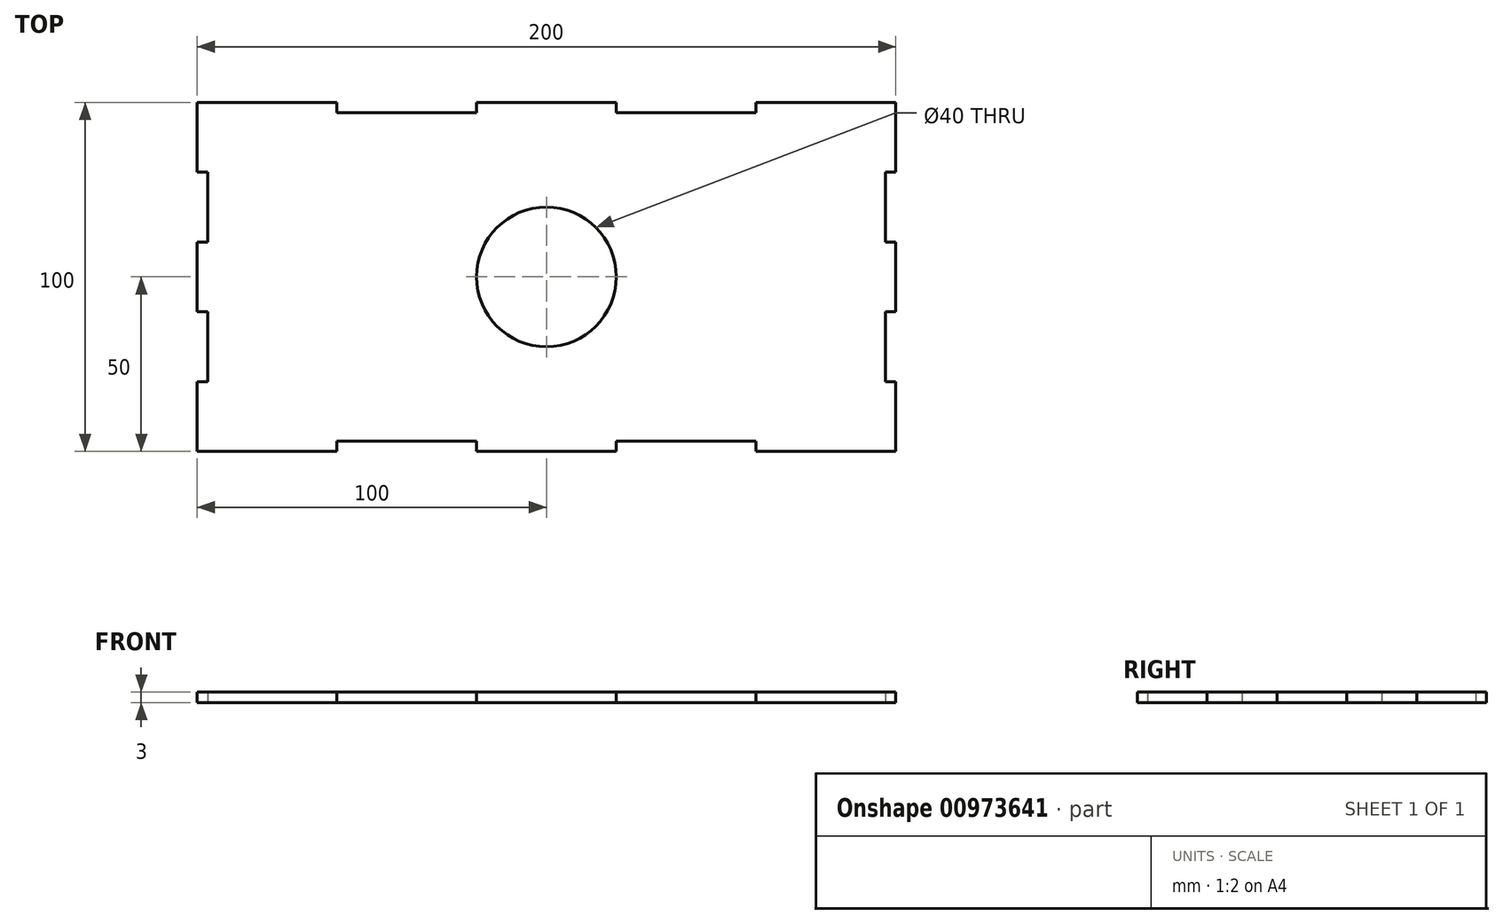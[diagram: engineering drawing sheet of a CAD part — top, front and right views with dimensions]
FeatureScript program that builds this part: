
annotation { "Feature Type Name" : "Feature", "Feature Type Description" : "" }
export const myFeature = defineFeature(function(context is Context, id is Id, definition is map)
    precondition{}
    {
        {
            var Q0;
            Q0=qCreatedBy(makeId("Top.planeOp"),FACE);
            var sketch = newSketch(context, id + "F0", { "sketchPlane" : qUnion([Q0])});
            skLineSegment(sketch, "E0", {"start": v(0, 0) * mm, "end": v(-200, 0) * mm});
            skLineSegment(sketch, "E1", {"start": v(-200, 0) * mm, "end": v(-200, -100) * mm});
            skLineSegment(sketch, "E2", {"start": v(-200, -100) * mm, "end": v(0, -100) * mm});
            skLineSegment(sketch, "E3", {"start": v(0, -100) * mm, "end": v(0, 0) * mm});
            skLineSegment(sketch, "E4", {"start": v(-200, -100) * mm, "end": v(-160, -100) * mm});
            skLineSegment(sketch, "E5", {"start": v(-120, -100) * mm, "end": v(-80, -100) * mm});
            skLineSegment(sketch, "E6", {"start": v(-200, 0) * mm, "end": v(-200, -20) * mm});
            skLineSegment(sketch, "E7", {"start": v(-200, -40) * mm, "end": v(-200, -60) * mm});
            skLineSegment(sketch, "E8", {"start": v(0, -40) * mm, "end": v(0, -60) * mm});
            skLineSegment(sketch, "E9", {"start": v(-160, -100) * mm, "end": v(-160, -97) * mm});
            skLineSegment(sketch, "E10", {"start": v(-160, -97) * mm, "end": v(-120, -97) * mm});
            skLineSegment(sketch, "E11", {"start": v(-80, -97) * mm, "end": v(-40, -97) * mm});
            skLineSegment(sketch, "E12", {"start": v(-200, -60) * mm, "end": v(-197, -60) * mm});
            skLineSegment(sketch, "E13", {"start": v(-197, -60) * mm, "end": v(-197, -80) * mm});
            skLineSegment(sketch, "E14", {"start": v(-197, -40) * mm, "end": v(-197, -20) * mm});
            skLineSegment(sketch, "E15", {"start": v(-160, 0) * mm, "end": v(-160, -3) * mm});
            skLineSegment(sketch, "E16", {"start": v(-160, -3) * mm, "end": v(-120, -3) * mm});
            skLineSegment(sketch, "E17", {"start": v(-80, -3) * mm, "end": v(-40, -3) * mm});
            skLineSegment(sketch, "E18", {"start": v(0, -20) * mm, "end": v(-3, -20) * mm});
            skLineSegment(sketch, "E19", {"start": v(-3, -20) * mm, "end": v(-3, -40) * mm});
            skLineSegment(sketch, "E20", {"start": v(-3, -60) * mm, "end": v(-3, -80) * mm});
            skLineSegment(sketch, "E21", {"start": v(-197, -20) * mm, "end": v(-200, -20) * mm});
            skLineSegment(sketch, "E22", {"start": v(-197, -40) * mm, "end": v(-200, -40) * mm});
            skLineSegment(sketch, "E23", {"start": v(-197, -80) * mm, "end": v(-200, -80) * mm});
            skLineSegment(sketch, "E24", {"start": v(-120, -97) * mm, "end": v(-120, -100) * mm});
            skLineSegment(sketch, "E25", {"start": v(-80, -97) * mm, "end": v(-80, -100) * mm});
            skLineSegment(sketch, "E26", {"start": v(-40, -97) * mm, "end": v(-40, -100) * mm});
            skLineSegment(sketch, "E27", {"start": v(-120, -3) * mm, "end": v(-120, 0) * mm});
            skLineSegment(sketch, "E28", {"start": v(-80, -3) * mm, "end": v(-80, 0) * mm});
            skLineSegment(sketch, "E29", {"start": v(-40, -3) * mm, "end": v(-40, 0) * mm});
            skLineSegment(sketch, "E30", {"start": v(-3, -40) * mm, "end": v(0, -40) * mm});
            skLineSegment(sketch, "E31", {"start": v(-3, -60) * mm, "end": v(0, -60) * mm});
            skLineSegment(sketch, "E32", {"start": v(-3, -80) * mm, "end": v(0, -80) * mm});
            skPoint(sketch, "E33.startSnap0", {"position": v(0, -50) * mm});
            skPoint(sketch, "E33.startSnap1", {"position": v(-100, 0) * mm});
            skCircle(sketch, "E34", {"center": v(-100, -50) * mm, "radius": 20 * mm});
            skSolve(sketch);
        }
        {
            var Q0;
            {var subQ1=sQuery(id+"F0.wireOp",EDGE,"E9");Q0=makeQuery(id+"F0.imprint","IMPRINT",FACE,{"disambiguationData":[TD([[makeQuery(id+"F0.imprint","IMPRINT",EDGE,{"derivedFrom":subQ1}),1.0]])]});}
            extrude(context, id + "F1", {"entities" : qUnion([Q0]), "depth" : 3 * mm, "offsetDistance" : 25 * mm});
        }
    });
